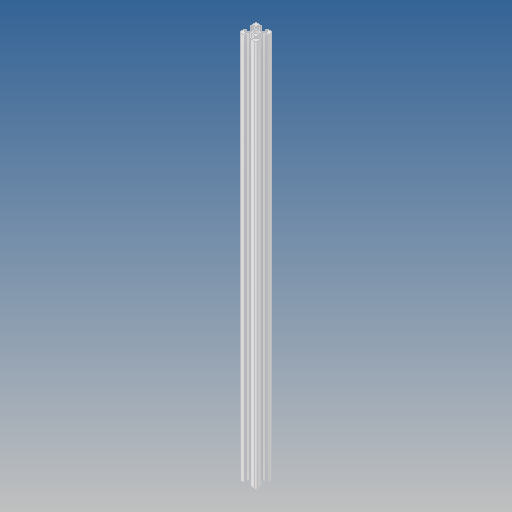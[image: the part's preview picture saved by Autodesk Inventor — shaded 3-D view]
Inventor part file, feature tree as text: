
AUTODESK INVENTOR PART (.ipt)
format: ipt  version: 2018 (Build 220112000, 112)  size: 247,296 bytes
history: native  units: mm
features: other x1, extrude x1, sketch x1, projected_geometry x1
ambient origin geometry x8: Origin, YZ Plane, XZ Plane, XY Plane, X Axis, Y Axis, Z Axis, Center Point
bodies: Solid1 (feature_tree), Body1 (feature_tree)
feature tree (4):
  other  "<userpath>\OneDrive\Objet3D\3DPrinter\Parameters.xlsx"
  extrude  "Extrusion1"  [1 undecoded]
  sketch  "Sketch1"  dims[d0=360.0mm d1=0.0mm]
  projected_geometry  "Projected Loop1"
note: 1 required parameter value undecoded (feature->parameter linkage not recoverable at this tier; creation-order binding heuristic only, values carry confidence <= 0.55)
